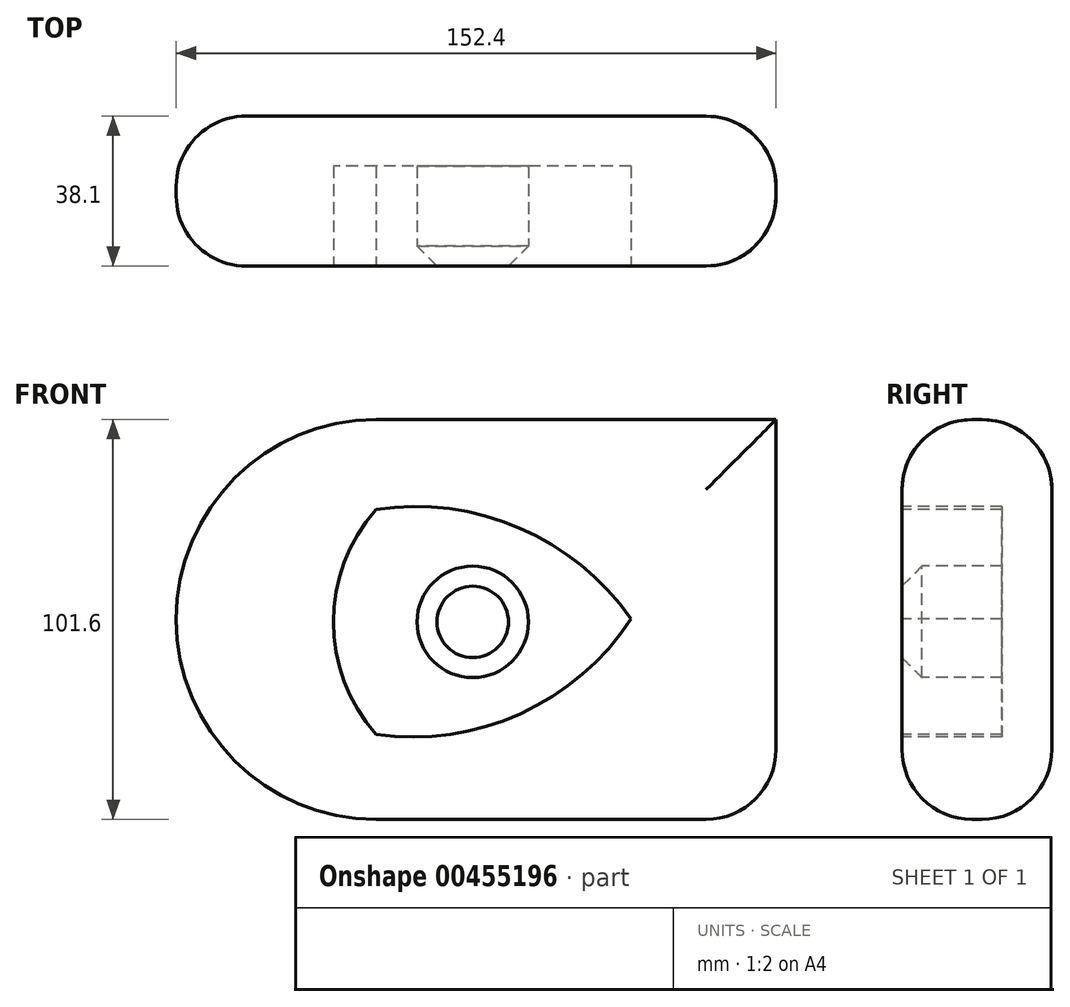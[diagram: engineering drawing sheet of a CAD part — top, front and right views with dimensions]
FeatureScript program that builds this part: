
annotation { "Feature Type Name" : "Feature", "Feature Type Description" : "" }
export const myFeature = defineFeature(function(context is Context, id is Id, definition is map)
    precondition{}
    {
        {
            var Q0;
            Q0=qCreatedBy(makeId("Front.planeOp"),FACE);
            var sketch = newSketch(context, id + "F0", { "sketchPlane" : qUnion([Q0])});
            skLineSegment(sketch, "E0.bottom", {"start": v(0, 0) * mm, "end": v(101.6, 0) * mm});
            skLineSegment(sketch, "E0.top", {"start": v(0, 101.6) * mm, "end": v(101.6, 101.6) * mm});
            skLineSegment(sketch, "E0.left", {"start": v(0, 0) * mm, "end": v(0, 101.6) * mm});
            skLineSegment(sketch, "E0.right", {"start": v(101.6, 0) * mm, "end": v(101.6, 101.6) * mm});
            skSolve(sketch);
        }
        {
            var Q0;
            Q0 = qSketchRegion(id + "F0", true);
            extrude(context, id + "F1", {"entities" : qUnion([Q0]), "depth" : 38.1 * mm});
        }
        {
            var Q0;
            Q0=makeQuery(id+"F1.opExtrude","CAP_FACE",FACE,{"disambiguationData":[OSD([sQuery(id+"F0.wireOp",EDGE,"E0.bottom"),sQuery(id+"F0.wireOp",EDGE,"E0.top"),sQuery(id+"F0.wireOp",EDGE,"E0.left"),sQuery(id+"F0.wireOp",EDGE,"E0.right")])],"isStart":false});
            var sketch = newSketch(context, id + "F2", { "sketchPlane" : qUnion([Q0])});
            skArc(sketch, "E1", {"start": v(0, 101.6) * mm, "mid": v(-50.8, 50.8) * mm, "end": v(0, 0) * mm});
            skSolve(sketch);
        }
        {
            var Q0;
            Q0=makeQuery(id+"F2.imprint","IMPRINT",FACE,{"disambiguationData":[TD([[makeQuery(id+"F2.imprint","IMPRINT",EDGE,{"derivedFrom":sQuery(id+"F2.wireOp",EDGE,"E1")}),1.0]])]});
            extrude(context, id + "F3", {"entities" : qUnion([Q0]), "operationType" : NewBodyOperationType.ADD, "oppositeDirection" : true, "depth" : 38.1 * mm});
        }
        {
            var Q0;
            Q0=makeQuery(id+"F1.opExtrude","CAP_EDGE",EDGE,{"disambiguationData":[OSD([sQuery(id+"F0.wireOp",EDGE,"E0.top")])],"isStart":false});
            var Q1;
            Q1=makeQuery(id+"F3.opExtrude","CAP_EDGE",EDGE,{"disambiguationData":[OSD([sQuery(id+"F2.wireOp",EDGE,"E1")])],"isStart":true});
            var Q2;
            Q2=makeQuery(id+"F1.opExtrude","CAP_EDGE",EDGE,{"disambiguationData":[OSD([sQuery(id+"F0.wireOp",EDGE,"E0.bottom")])],"isStart":false});
            var Q3;
            Q3=makeQuery(id+"F1.opExtrude","CAP_EDGE",EDGE,{"disambiguationData":[OSD([sQuery(id+"F0.wireOp",EDGE,"E0.right")])],"isStart":false});
            var Q4;
            Q4=makeQuery(id+"F1.opExtrude","CAP_EDGE",EDGE,{"disambiguationData":[OSD([sQuery(id+"F0.wireOp",EDGE,"E0.right")])],"isStart":true});
            var Q5;
            Q5=makeQuery(id+"F1.opExtrude","SWEPT_FACE",FACE,{"disambiguationData":[OSD([sQuery(id+"F0.wireOp",EDGE,"E0.bottom")])]});
            var Q6;
            Q6=makeQuery(id+"F1.opExtrude","CAP_EDGE",EDGE,{"disambiguationData":[OSD([sQuery(id+"F0.wireOp",EDGE,"E0.bottom")])],"isStart":true});
            var Q7;
            Q7=makeQuery(id+"F3.opExtrude","CAP_EDGE",EDGE,{"disambiguationData":[OSD([sQuery(id+"F2.wireOp",EDGE,"E1")])],"isStart":false});
            var Q8;
            Q8=makeQuery(id+"F1.opExtrude","CAP_EDGE",EDGE,{"disambiguationData":[OSD([sQuery(id+"F0.wireOp",EDGE,"E0.top")])],"isStart":true});
            fillet(context, id + "F4", {"entities" : qUnion([Q0, Q1, Q2, Q3, Q4, Q5, Q6, Q7, Q8]), "radius" : 17.78 * mm, "tangentPropagation" : true, "allowEdgeOverflow" : false});
        }
        {
            var Q0;
            {var subQ0=sQuery(id+"F0.wireOp",EDGE,"E0.left");Q0=makeQuery(id+"F3.boolean.opBoolean","MERGE",FACE,{"derivedFrom":[makeQuery(id+"F1.opExtrude","CAP_FACE",FACE,{"disambiguationData":[OSD([sQuery(id+"F0.wireOp",EDGE,"E0.bottom"),sQuery(id+"F0.wireOp",EDGE,"E0.top"),subQ0,sQuery(id+"F0.wireOp",EDGE,"E0.right")])],"isStart":false}),makeQuery(id+"F3.opExtrude","CAP_FACE",FACE,{"disambiguationData":[OSD([subQ0,sQuery(id+"F2.wireOp",EDGE,"E1")])],"isStart":true})]});}
            var sketch = newSketch(context, id + "F5", { "sketchPlane" : qUnion([Q0])});
            skArc(sketch, "E2", {"start": v(0, 78.78) * mm, "mid": v(-10.84, 50.18) * mm, "end": v(0, 21.58) * mm});
            skArc(sketch, "E3", {"start": v(0, 21.58) * mm, "mid": v(36.65, 26.85) * mm, "end": v(64.75, 50.95) * mm});
            skArc(sketch, "E4", {"start": v(64.75, 50.95) * mm, "mid": v(36.33, 74.07) * mm, "end": v(0, 78.78) * mm});
            skCircle(sketch, "E5", {"center": v(24.54, 50.18) * mm, "radius": 14.16 * mm});
            skSolve(sketch);
        }
        {
            var Q0;
            Q0=makeQuery(id+"F5.imprint","IMPRINT",FACE,{"disambiguationData":[TD([[makeQuery(id+"F5.imprint","IMPRINT",EDGE,{"derivedFrom":sQuery(id+"F5.wireOp",EDGE,"E2")}),1.0]])]});
            extrude(context, id + "F6", {"entities" : qUnion([Q0]), "operationType" : NewBodyOperationType.REMOVE, "oppositeDirection" : true, "depth" : 25.4 * mm});
        }
        {
            var Q0;
            Q0=makeQuery(id+"F6.boolean.opBoolean","COPY",EDGE,{"derivedFrom":makeQuery(id+"F6.opExtrude","CAP_EDGE",EDGE,{"disambiguationData":[OSD([sQuery(id+"F5.wireOp",EDGE,"E5")])],"isStart":true})});
            var Q1;
            Q1=makeQuery(id+"F6.boolean.opBoolean","COPY",EDGE,{"derivedFrom":makeQuery(id+"F6.opExtrude","CAP_EDGE",EDGE,{"disambiguationData":[OSD([sQuery(id+"F5.wireOp",EDGE,"E2")])],"isStart":true})});
            var Q2;
            Q2=makeQuery(id+"F6.boolean.opBoolean","COPY",EDGE,{"derivedFrom":makeQuery(id+"F6.opExtrude","CAP_EDGE",EDGE,{"disambiguationData":[OSD([sQuery(id+"F5.wireOp",EDGE,"E4")])],"isStart":true})});
            var Q3;
            Q3=makeQuery(id+"F6.boolean.opBoolean","COPY",EDGE,{"derivedFrom":makeQuery(id+"F6.opExtrude","CAP_EDGE",EDGE,{"disambiguationData":[OSD([sQuery(id+"F5.wireOp",EDGE,"E3")])],"isStart":true})});
            chamfer(context, id + "F7", {"entities" : qUnion([Q0, Q1, Q2, Q3]), "width" : 5.08 * mm, "tangentPropagation" : true});
        }
    });
